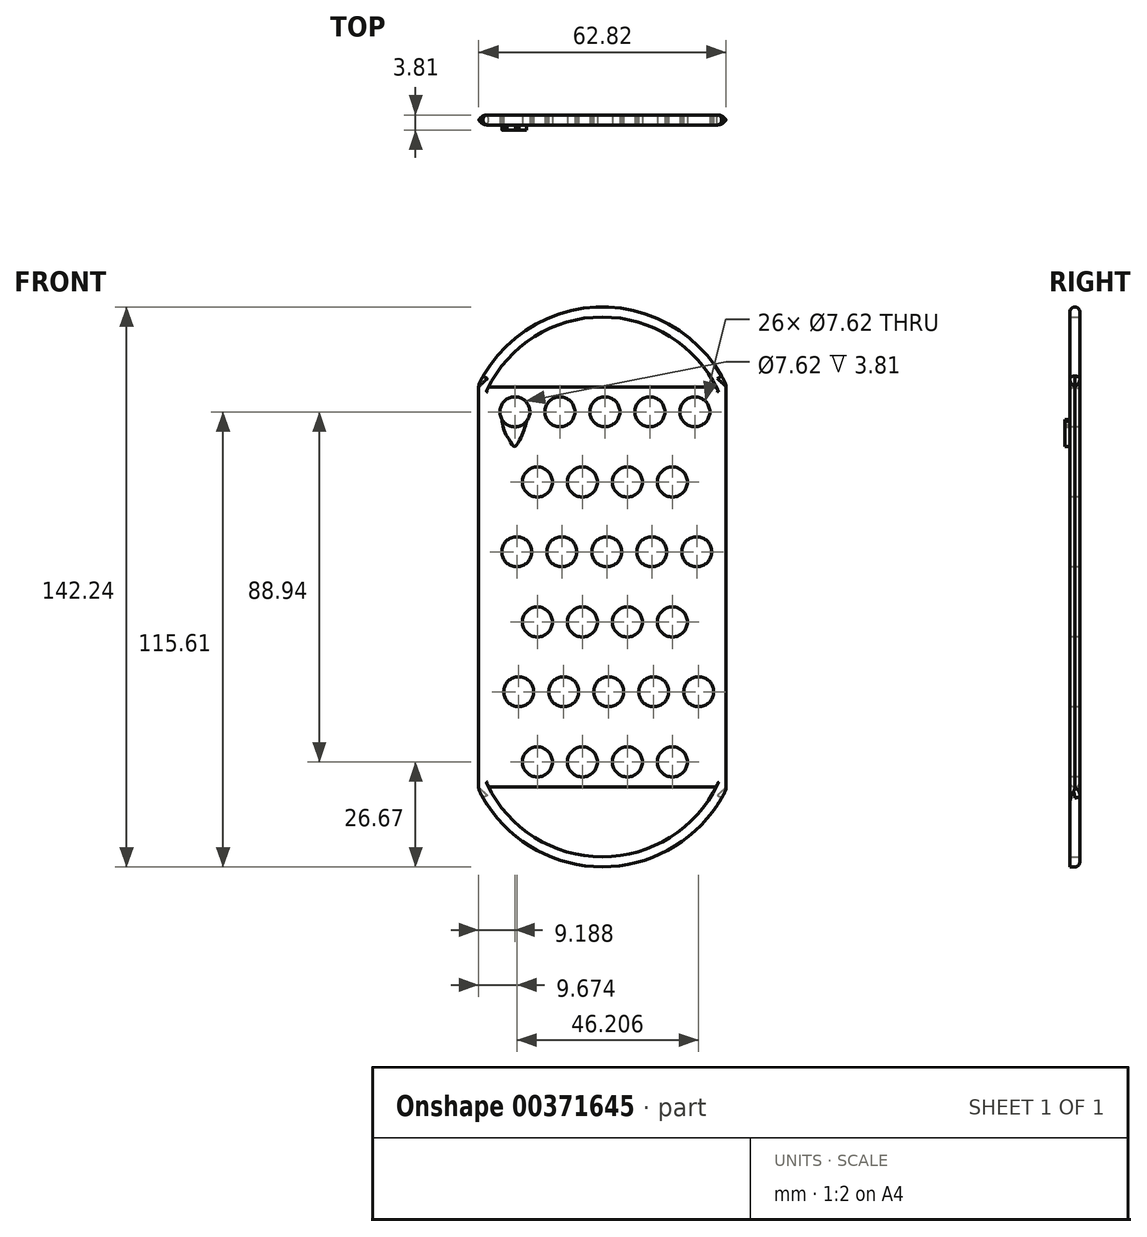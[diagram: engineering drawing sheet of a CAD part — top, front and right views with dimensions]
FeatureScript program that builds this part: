
annotation { "Feature Type Name" : "Feature", "Feature Type Description" : "" }
export const myFeature = defineFeature(function(context is Context, id is Id, definition is map)
    precondition{}
    {
        {
            var Q0;
            Q0=qCreatedBy(makeId("Front.planeOp"),FACE);
            var sketch = newSketch(context, id + "F0", { "sketchPlane" : qUnion([Q0])});
            skLineSegment(sketch, "E0.bottom", {"start": v(-31.75, 50.8) * mm, "end": v(31.75, 50.8) * mm});
            skLineSegment(sketch, "E0.top", {"start": v(-31.75, -50.8) * mm, "end": v(31.75, -50.8) * mm});
            skLineSegment(sketch, "E0.left", {"start": v(-31.75, 50.8) * mm, "end": v(-31.75, -50.8) * mm});
            skLineSegment(sketch, "E0.right", {"start": v(31.75, 50.8) * mm, "end": v(31.75, -50.8) * mm});
            skPoint(sketch, "E0.middle", {"position": v(0, 0) * mm});
            skSolve(sketch);
        }
        {
            var Q0;
            Q0=makeQuery(id+"F0.imprint","IMPRINT",FACE,{"disambiguationData":[TD([[makeQuery(id+"F0.imprint","IMPRINT",EDGE,{"derivedFrom":sQuery(id+"F0.wireOp",EDGE,"E0.bottom")}),-1.0]])]});
            extrude(context, id + "F1", {"entities" : qUnion([Q0]), "depth" : 2.54 * mm});
        }
        {
            var Q0;
            Q0=qCreatedBy(makeId("Front.planeOp"),FACE);
            var sketch = newSketch(context, id + "F2", { "sketchPlane" : qUnion([Q0])});
            skArc(sketch, "E1", {"start": v(31.75, 50.8) * mm, "mid": v(0, 71.12) * mm, "end": v(-31.75, 50.8) * mm});
            skLineSegment(sketch, "E2", {"start": v(-32.28, 0) * mm, "end": v(31.73, 0) * mm, "construction": true});
            skArc(sketch, "E3.MirrorCS", {"start": v(31.75, -50.8) * mm, "mid": v(0, -71.12) * mm, "end": v(-31.75, -50.8) * mm});
            skArc(sketch, "E4.0", {"start": v(28.93, 50.8) * mm, "mid": v(0, 68.58) * mm, "end": v(-28.93, 50.8) * mm});
            skLineSegment(sketch, "E5", {"start": v(-31.75, 50.8) * mm, "end": v(-28.93, 50.8) * mm});
            skLineSegment(sketch, "E6", {"start": v(31.75, 50.8) * mm, "end": v(28.93, 50.8) * mm});
            skArc(sketch, "E7.MirrorCS", {"start": v(28.93, -50.8) * mm, "mid": v(0, -68.58) * mm, "end": v(-28.93, -50.8) * mm});
            skLineSegment(sketch, "E8.MirrorCS", {"start": v(-31.75, -50.8) * mm, "end": v(-28.93, -50.8) * mm});
            skLineSegment(sketch, "E9.MirrorCS", {"start": v(31.75, -50.8) * mm, "end": v(28.93, -50.8) * mm});
            skSolve(sketch);
        }
        {
            var Q0;
            Q0 = qSketchRegion(id + "F2", true);
            extrude(context, id + "F3", {"entities" : qUnion([Q0]), "operationType" : NewBodyOperationType.ADD, "depth" : 2.54 * mm});
        }
        {
            var Q0;
            Q0=makeQuery(id+"F1.opExtrude","CAP_EDGE",EDGE,{"disambiguationData":[OSD([sQuery(id+"F0.wireOp",EDGE,"E0.left")])],"isStart":true});
            var Q1;
            Q1=makeQuery(id+"F1.opExtrude","CAP_EDGE",EDGE,{"disambiguationData":[OSD([sQuery(id+"F0.wireOp",EDGE,"E0.right")])],"isStart":true});
            var Q2;
            Q2=makeQuery(id+"F1.opExtrude","CAP_EDGE",EDGE,{"disambiguationData":[OSD([sQuery(id+"F0.wireOp",EDGE,"E0.left")])],"isStart":false});
            var Q3;
            Q3=makeQuery(id+"F1.opExtrude","CAP_EDGE",EDGE,{"disambiguationData":[OSD([sQuery(id+"F0.wireOp",EDGE,"E0.right")])],"isStart":false});
            fillet(context, id + "F4", {"entities" : qUnion([Q0, Q1, Q2, Q3]), "radius" : 2.54 * mm, "tangentPropagation" : true, "allowEdgeOverflow" : false});
        }
        {
            var Q0;
            Q0=makeQuery(id+"F3.opExtrude","CAP_EDGE",EDGE,{"disambiguationData":[OSD([sQuery(id+"F2.wireOp",EDGE,"E3.MirrorCS")])],"isStart":true});
            var Q1;
            Q1=makeQuery(id+"F3.opExtrude","CAP_EDGE",EDGE,{"disambiguationData":[OSD([sQuery(id+"F2.wireOp",EDGE,"E1")])],"isStart":true});
            var Q2;
            Q2=makeQuery(id+"F1.opExtrude","CAP_EDGE",EDGE,{"disambiguationData":[OSD([sQuery(id+"F0.wireOp",EDGE,"E0.bottom")])],"isStart":true});
            var Q3;
            Q3=makeQuery(id+"F1.opExtrude","CAP_EDGE",EDGE,{"disambiguationData":[OSD([sQuery(id+"F0.wireOp",EDGE,"E0.top")])],"isStart":true});
            var Q4;
            Q4=makeQuery(id+"F3.opExtrude","CAP_EDGE",EDGE,{"disambiguationData":[OSD([sQuery(id+"F2.wireOp",EDGE,"E1")])],"isStart":false});
            var Q5;
            Q5=makeQuery(id+"F1.opExtrude","CAP_EDGE",EDGE,{"disambiguationData":[OSD([sQuery(id+"F0.wireOp",EDGE,"E0.bottom")])],"isStart":false});
            var Q6;
            Q6=makeQuery(id+"F1.opExtrude","CAP_EDGE",EDGE,{"disambiguationData":[OSD([sQuery(id+"F0.wireOp",EDGE,"E0.top")])],"isStart":false});
            fillet(context, id + "F5", {"entities" : qUnion([Q0, Q1, Q2, Q3, Q4, Q5, Q6]), "radius" : 1.27 * mm, "tangentPropagation" : true, "allowEdgeOverflow" : false});
        }
        {
            var Q0;
            Q0=makeQuery(id+"F5.opFillet","SPLIT",FACE,{"disambiguationData":[OD(1.0)],"derivedFrom":makeQuery(id+"F3.boolean.opBoolean","MERGE",FACE,{"derivedFrom":[makeQuery(id+"F1.opExtrude","CAP_FACE",FACE,{"disambiguationData":[OSD([sQuery(id+"F0.wireOp",EDGE,"E0.bottom"),sQuery(id+"F0.wireOp",EDGE,"E0.top"),sQuery(id+"F0.wireOp",EDGE,"E0.left"),sQuery(id+"F0.wireOp",EDGE,"E0.right")])],"isStart":false}),makeQuery(id+"F3.opExtrude","CAP_FACE",FACE,{"disambiguationData":[OSD([sQuery(id+"F2.wireOp",EDGE,"E1"),sQuery(id+"F2.wireOp",EDGE,"E4.0"),sQuery(id+"F2.wireOp",EDGE,"E5"),sQuery(id+"F2.wireOp",EDGE,"E6")])],"isStart":false}),makeQuery(id+"F3.opExtrude","CAP_FACE",FACE,{"disambiguationData":[OSD([sQuery(id+"F2.wireOp",EDGE,"E3.MirrorCS"),sQuery(id+"F2.wireOp",EDGE,"E7.MirrorCS"),sQuery(id+"F2.wireOp",EDGE,"E8.MirrorCS"),sQuery(id+"F2.wireOp",EDGE,"E9.MirrorCS")])],"isStart":false})]})});
            var sketch = newSketch(context, id + "F6", { "sketchPlane" : qUnion([Q0])});
            skCircle(sketch, "E10", {"center": v(-22.22, 44.5) * mm, "radius": 3.81 * mm});
            skCircle(sketch, "E11.1.0.0", {"center": v(-10.8, 44.5) * mm, "radius": 3.81 * mm});
            skCircle(sketch, "E11.2.0.0", {"center": v(0.64, 44.5) * mm, "radius": 3.81 * mm});
            skCircle(sketch, "E11.3.0.0", {"center": v(12.07, 44.5) * mm, "radius": 3.81 * mm});
            skCircle(sketch, "E11.4.0.0", {"center": v(23.5, 44.5) * mm, "radius": 3.81 * mm});
            skLineSegment(sketch, "E11.direction1", {"start": v(-22.22, 44.5) * mm, "end": v(-10.8, 44.5) * mm, "construction": true});
            skLineSegment(sketch, "E12.direction1", {"start": v(0.64, 44.5) * mm, "end": v(-24.64, 44.5) * mm, "construction": true});
            skCircle(sketch, "E13", {"center": v(-16.5, -44.45) * mm, "radius": 3.81 * mm});
            skCircle(sketch, "E14.1.0.0", {"center": v(-5.08, -44.45) * mm, "radius": 3.81 * mm});
            skCircle(sketch, "E14.2.0.0", {"center": v(6.35, -44.45) * mm, "radius": 3.81 * mm});
            skLineSegment(sketch, "E14.direction1", {"start": v(-16.5, -44.45) * mm, "end": v(-5.08, -44.45) * mm, "construction": true});
            skCircle(sketch, "E15.0.3.0", {"center": v(17.78, -44.45) * mm, "radius": 3.81 * mm});
            skCircle(sketch, "E16.0.1.0", {"center": v(1.12, 8.93) * mm, "radius": 3.81 * mm});
            skCircle(sketch, "E16.0.1.1", {"center": v(-10.3, 8.93) * mm, "radius": 3.81 * mm});
            skCircle(sketch, "E16.0.1.2", {"center": v(-21.74, 8.93) * mm, "radius": 3.81 * mm});
            skLineSegment(sketch, "E16.0.1.3", {"start": v(1.12, 8.93) * mm, "end": v(-24.16, 8.93) * mm, "construction": true});
            skLineSegment(sketch, "E16.0.1.4", {"start": v(-21.74, 8.93) * mm, "end": v(-10.3, 8.93) * mm, "construction": true});
            skCircle(sketch, "E16.0.1.5", {"center": v(23.98, 8.93) * mm, "radius": 3.81 * mm});
            skCircle(sketch, "E16.0.1.6", {"center": v(12.55, 8.93) * mm, "radius": 3.81 * mm});
            skCircle(sketch, "E16.0.2.0", {"center": v(1.61, -26.62) * mm, "radius": 3.81 * mm});
            skCircle(sketch, "E16.0.2.1", {"center": v(-9.82, -26.62) * mm, "radius": 3.81 * mm});
            skCircle(sketch, "E16.0.2.2", {"center": v(-21.25, -26.62) * mm, "radius": 3.81 * mm});
            skLineSegment(sketch, "E16.0.2.3", {"start": v(1.61, -26.62) * mm, "end": v(-23.67, -26.62) * mm, "construction": true});
            skLineSegment(sketch, "E16.0.2.4", {"start": v(-21.25, -26.62) * mm, "end": v(-9.82, -26.62) * mm, "construction": true});
            skCircle(sketch, "E16.0.2.5", {"center": v(24.47, -26.62) * mm, "radius": 3.81 * mm});
            skCircle(sketch, "E16.0.2.6", {"center": v(13.04, -26.62) * mm, "radius": 3.81 * mm});
            skLineSegment(sketch, "E16.direction1", {"start": v(-24.64, 44.5) * mm, "end": v(1.4, 44.5) * mm, "construction": true});
            skLineSegment(sketch, "E16.direction2", {"start": v(-24.64, 44.5) * mm, "end": v(-24.16, 8.93) * mm, "construction": true});
            skCircle(sketch, "E17.0.1.0", {"center": v(-16.5, -8.89) * mm, "radius": 3.81 * mm});
            skCircle(sketch, "E17.0.1.1", {"center": v(-5.08, -8.89) * mm, "radius": 3.81 * mm});
            skCircle(sketch, "E17.0.1.2", {"center": v(6.35, -8.89) * mm, "radius": 3.81 * mm});
            skCircle(sketch, "E17.0.1.3", {"center": v(17.78, -8.89) * mm, "radius": 3.81 * mm});
            skCircle(sketch, "E17.0.2.0", {"center": v(-16.5, 26.67) * mm, "radius": 3.81 * mm});
            skCircle(sketch, "E17.0.2.1", {"center": v(-5.08, 26.67) * mm, "radius": 3.81 * mm});
            skCircle(sketch, "E17.0.2.2", {"center": v(6.35, 26.67) * mm, "radius": 3.81 * mm});
            skCircle(sketch, "E17.0.2.3", {"center": v(17.78, 26.67) * mm, "radius": 3.81 * mm});
            skLineSegment(sketch, "E17.direction1", {"start": v(-16.5, -44.45) * mm, "end": v(-4.7, -12.32) * mm, "construction": true});
            skLineSegment(sketch, "E17.direction2", {"start": v(-16.5, -44.45) * mm, "end": v(-16.5, -8.89) * mm, "construction": true});
            skSolve(sketch);
        }
        {
            var Q0;
            Q0=makeQuery(id+"F6.imprint","IMPRINT",FACE,{"disambiguationData":[TD([[makeQuery(id+"F6.imprint","IMPRINT",EDGE,{"derivedFrom":sQuery(id+"F6.wireOp",EDGE,"E10")}),1.0]])]});
            var Q1;
            Q1=makeQuery(id+"F6.imprint","IMPRINT",FACE,{"disambiguationData":[TD([[makeQuery(id+"F6.imprint","IMPRINT",EDGE,{"derivedFrom":sQuery(id+"F6.wireOp",EDGE,"E11.1.0.0")}),1.0]])]});
            var Q2;
            Q2=makeQuery(id+"F6.imprint","IMPRINT",FACE,{"disambiguationData":[TD([[makeQuery(id+"F6.imprint","IMPRINT",EDGE,{"derivedFrom":sQuery(id+"F6.wireOp",EDGE,"E11.2.0.0")}),1.0]])]});
            var Q3;
            Q3=makeQuery(id+"F6.imprint","IMPRINT",FACE,{"disambiguationData":[TD([[makeQuery(id+"F6.imprint","IMPRINT",EDGE,{"derivedFrom":sQuery(id+"F6.wireOp",EDGE,"E11.3.0.0")}),1.0]])]});
            var Q4;
            Q4=makeQuery(id+"F6.imprint","IMPRINT",FACE,{"disambiguationData":[TD([[makeQuery(id+"F6.imprint","IMPRINT",EDGE,{"derivedFrom":sQuery(id+"F6.wireOp",EDGE,"E11.4.0.0")}),1.0]])]});
            var Q5;
            Q5=makeQuery(id+"F6.imprint","IMPRINT",FACE,{"disambiguationData":[TD([[makeQuery(id+"F6.imprint","IMPRINT",EDGE,{"derivedFrom":sQuery(id+"F6.wireOp",EDGE,"E17.0.2.3")}),1.0]])]});
            var Q6;
            Q6=makeQuery(id+"F6.imprint","IMPRINT",FACE,{"disambiguationData":[TD([[makeQuery(id+"F6.imprint","IMPRINT",EDGE,{"derivedFrom":sQuery(id+"F6.wireOp",EDGE,"E17.0.2.2")}),1.0]])]});
            var Q7;
            Q7=makeQuery(id+"F6.imprint","IMPRINT",FACE,{"disambiguationData":[TD([[makeQuery(id+"F6.imprint","IMPRINT",EDGE,{"derivedFrom":sQuery(id+"F6.wireOp",EDGE,"E17.0.2.1")}),1.0]])]});
            var Q8;
            Q8=makeQuery(id+"F6.imprint","IMPRINT",FACE,{"disambiguationData":[TD([[makeQuery(id+"F6.imprint","IMPRINT",EDGE,{"derivedFrom":sQuery(id+"F6.wireOp",EDGE,"E17.0.2.0")}),1.0]])]});
            var Q9;
            Q9=makeQuery(id+"F6.imprint","IMPRINT",FACE,{"disambiguationData":[TD([[makeQuery(id+"F6.imprint","IMPRINT",EDGE,{"derivedFrom":sQuery(id+"F6.wireOp",EDGE,"E16.0.1.2")}),1.0]])]});
            var Q10;
            Q10=makeQuery(id+"F6.imprint","IMPRINT",FACE,{"disambiguationData":[TD([[makeQuery(id+"F6.imprint","IMPRINT",EDGE,{"derivedFrom":sQuery(id+"F6.wireOp",EDGE,"E16.0.1.1")}),1.0]])]});
            var Q11;
            Q11=makeQuery(id+"F6.imprint","IMPRINT",FACE,{"disambiguationData":[TD([[makeQuery(id+"F6.imprint","IMPRINT",EDGE,{"derivedFrom":sQuery(id+"F6.wireOp",EDGE,"E16.0.1.0")}),1.0]])]});
            var Q12;
            Q12=makeQuery(id+"F6.imprint","IMPRINT",FACE,{"disambiguationData":[TD([[makeQuery(id+"F6.imprint","IMPRINT",EDGE,{"derivedFrom":sQuery(id+"F6.wireOp",EDGE,"E16.0.1.6")}),1.0]])]});
            var Q13;
            Q13=makeQuery(id+"F6.imprint","IMPRINT",FACE,{"disambiguationData":[TD([[makeQuery(id+"F6.imprint","IMPRINT",EDGE,{"derivedFrom":sQuery(id+"F6.wireOp",EDGE,"E16.0.1.5")}),1.0]])]});
            var Q14;
            Q14=makeQuery(id+"F6.imprint","IMPRINT",FACE,{"disambiguationData":[TD([[makeQuery(id+"F6.imprint","IMPRINT",EDGE,{"derivedFrom":sQuery(id+"F6.wireOp",EDGE,"E17.0.1.3")}),1.0]])]});
            var Q15;
            Q15=makeQuery(id+"F6.imprint","IMPRINT",FACE,{"disambiguationData":[TD([[makeQuery(id+"F6.imprint","IMPRINT",EDGE,{"derivedFrom":sQuery(id+"F6.wireOp",EDGE,"E17.0.1.2")}),1.0]])]});
            var Q16;
            Q16=makeQuery(id+"F6.imprint","IMPRINT",FACE,{"disambiguationData":[TD([[makeQuery(id+"F6.imprint","IMPRINT",EDGE,{"derivedFrom":sQuery(id+"F6.wireOp",EDGE,"E17.0.1.1")}),1.0]])]});
            var Q17;
            Q17=makeQuery(id+"F6.imprint","IMPRINT",FACE,{"disambiguationData":[TD([[makeQuery(id+"F6.imprint","IMPRINT",EDGE,{"derivedFrom":sQuery(id+"F6.wireOp",EDGE,"E17.0.1.0")}),1.0]])]});
            var Q18;
            Q18=makeQuery(id+"F6.imprint","IMPRINT",FACE,{"disambiguationData":[TD([[makeQuery(id+"F6.imprint","IMPRINT",EDGE,{"derivedFrom":sQuery(id+"F6.wireOp",EDGE,"E16.0.2.2")}),1.0]])]});
            var Q19;
            Q19=makeQuery(id+"F6.imprint","IMPRINT",FACE,{"disambiguationData":[TD([[makeQuery(id+"F6.imprint","IMPRINT",EDGE,{"derivedFrom":sQuery(id+"F6.wireOp",EDGE,"E16.0.2.1")}),1.0]])]});
            var Q20;
            Q20=makeQuery(id+"F6.imprint","IMPRINT",FACE,{"disambiguationData":[TD([[makeQuery(id+"F6.imprint","IMPRINT",EDGE,{"derivedFrom":sQuery(id+"F6.wireOp",EDGE,"E16.0.2.0")}),1.0]])]});
            var Q21;
            Q21=makeQuery(id+"F6.imprint","IMPRINT",FACE,{"disambiguationData":[TD([[makeQuery(id+"F6.imprint","IMPRINT",EDGE,{"derivedFrom":sQuery(id+"F6.wireOp",EDGE,"E16.0.2.6")}),1.0]])]});
            var Q22;
            Q22=makeQuery(id+"F6.imprint","IMPRINT",FACE,{"disambiguationData":[TD([[makeQuery(id+"F6.imprint","IMPRINT",EDGE,{"derivedFrom":sQuery(id+"F6.wireOp",EDGE,"E16.0.2.5")}),1.0]])]});
            var Q23;
            Q23=makeQuery(id+"F6.imprint","IMPRINT",FACE,{"disambiguationData":[TD([[makeQuery(id+"F6.imprint","IMPRINT",EDGE,{"derivedFrom":sQuery(id+"F6.wireOp",EDGE,"E15.0.3.0")}),1.0]])]});
            var Q24;
            Q24=makeQuery(id+"F6.imprint","IMPRINT",FACE,{"disambiguationData":[TD([[makeQuery(id+"F6.imprint","IMPRINT",EDGE,{"derivedFrom":sQuery(id+"F6.wireOp",EDGE,"E14.2.0.0")}),1.0]])]});
            var Q25;
            Q25=makeQuery(id+"F6.imprint","IMPRINT",FACE,{"disambiguationData":[TD([[makeQuery(id+"F6.imprint","IMPRINT",EDGE,{"derivedFrom":sQuery(id+"F6.wireOp",EDGE,"E14.1.0.0")}),1.0]])]});
            var Q26;
            Q26=makeQuery(id+"F6.imprint","IMPRINT",FACE,{"disambiguationData":[TD([[makeQuery(id+"F6.imprint","IMPRINT",EDGE,{"derivedFrom":sQuery(id+"F6.wireOp",EDGE,"E13")}),1.0]])]});
            extrude(context, id + "F7", {"entities" : qUnion([Q0, Q1, Q2, Q3, Q4, Q5, Q6, Q7, Q8, Q9, Q10, Q11, Q12, Q13, Q14, Q15, Q16, Q17, Q18, Q19, Q20, Q21, Q22, Q23, Q24, Q25, Q26]), "operationType" : NewBodyOperationType.REMOVE, "oppositeDirection" : true, "depth" : 25.4 * mm});
        }
        {
            var Q0;
            Q0=makeQuery(id+"F5.opFillet","SPLIT",FACE,{"disambiguationData":[OD(1.0)],"derivedFrom":makeQuery(id+"F3.boolean.opBoolean","MERGE",FACE,{"derivedFrom":[makeQuery(id+"F1.opExtrude","CAP_FACE",FACE,{"disambiguationData":[OSD([sQuery(id+"F0.wireOp",EDGE,"E0.bottom"),sQuery(id+"F0.wireOp",EDGE,"E0.top"),sQuery(id+"F0.wireOp",EDGE,"E0.left"),sQuery(id+"F0.wireOp",EDGE,"E0.right")])],"isStart":false}),makeQuery(id+"F3.opExtrude","CAP_FACE",FACE,{"disambiguationData":[OSD([sQuery(id+"F2.wireOp",EDGE,"E1"),sQuery(id+"F2.wireOp",EDGE,"E4.0"),sQuery(id+"F2.wireOp",EDGE,"E5"),sQuery(id+"F2.wireOp",EDGE,"E6")])],"isStart":false}),makeQuery(id+"F3.opExtrude","CAP_FACE",FACE,{"disambiguationData":[OSD([sQuery(id+"F2.wireOp",EDGE,"E3.MirrorCS"),sQuery(id+"F2.wireOp",EDGE,"E7.MirrorCS"),sQuery(id+"F2.wireOp",EDGE,"E8.MirrorCS"),sQuery(id+"F2.wireOp",EDGE,"E9.MirrorCS")])],"isStart":false})]})});
            var sketch = newSketch(context, id + "F8", { "sketchPlane" : qUnion([Q0])});
            skFitSpline(sketch, "E18", {"points": [v(-22.28, 40.68) * mm, v(-21.14, 40.84) * mm, v(-19.2, 42.16) * mm], "startDerivative": vector(2.65, 0.01) * mm, "endDerivative": vector(3.44, 2.8) * mm});
            skFitSpline(sketch, "E19", {"points": [v(-22.28, 40.68) * mm, v(-23.14, 40.8) * mm, v(-24.16, 41.21) * mm, v(-25, 41.89) * mm, v(-25.48, 42.52) * mm, v(-25.02, 39.96) * mm, v(-23.8, 37.6) * mm, v(-22.28, 35.68) * mm, v(-20.9, 37.6) * mm, v(-19.88, 40.03) * mm, v(-19.2, 42.16) * mm], "startDerivative": vector(-12.13, 0.7) * mm, "endDerivative": vector(5.67, 19.15) * mm});
            skSolve(sketch);
        }
        {
            var Q0;
            {var subQ1=sQuery(id+"F8.wireOp",EDGE,"E18");var subQ2=makeQuery(id+"F7.boolean.opBoolean","COPY",EDGE,{"derivedFrom":makeQuery(id+"F7.opExtrude","CAP_EDGE",EDGE,{"disambiguationData":[OSD([sQuery(id+"F6.wireOp",EDGE,"E10")])],"isStart":true})});var subQ11=makeQuery(id+"F8.imprint","INTERSECT",VERTEX,{"disambiguationData":[OD(0.0)],"derivedFrom":[subQ2,subQ1]});Q0=makeQuery(id+"F8.imprint","IMPRINT",FACE,{"disambiguationData":[TD([[makeQuery(id+"F8.imprint","IMPRINT",EDGE,{"disambiguationData":[TD([[subQ11,-1.0]])],"derivedFrom":subQ1}),-1.0]])]});}
            extrude(context, id + "F9", {"entities" : qUnion([Q0]), "operationType" : NewBodyOperationType.ADD, "depth" : 1.27 * mm});
        }
    });
